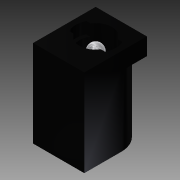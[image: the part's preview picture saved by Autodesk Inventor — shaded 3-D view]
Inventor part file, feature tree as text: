
AUTODESK INVENTOR PART (.ipt)
format: ipt  version: 2014 SP1 (Build 180222100, 222)  size: 133,632 bytes
history: native  units: mm
features: extrude x5, sketch x5, fillet x1
ambient origin geometry x8: Origin, YZ Plane, XZ Plane, XY Plane, X Axis, Y Axis, Z Axis, Center Point
bodies: Solid1 (feature_tree)
feature tree (11):
  extrude  "Extrusion1"  TaperAngle=0.0deg  [1 undecoded]
  extrude  "Extrusion2"  Depth=4.5mm
  extrude  "Extrusion4"  Depth=15.3mm
  extrude  "Extrusion3"  Depth=10.0mm TaperAngle=0.0deg
  fillet  "Fillet1"  Radius=2.5mm
  extrude  "Extrusion5"  Depth=1.25mm
  sketch  "Sketch1"  dims[d0=9.0mm d1=0.0mm]
  sketch  "Sketch2"  dims[d2=11.0mm d3=4.5mm]
  sketch  "Sketch3"  dims[d4=15.3mm d5=0.0mm d6=5.7mm]
  sketch  "Sketch4"  dims[d7=6.5mm d8=10.0mm d9=0.0mm d10=2.5mm]
  sketch  "Sketch5"  dims[d11=9.0mm d12=0.0mm d13=1.25mm d14=7.0mm d15=1.5mm d16=1.5mm d17=3.5mm d18=3.0mm d19=1.5mm d20=2.0mm d21=0.0mm d22=0.0mm d23=9.0mm d24=12.3mm d25=0.0mm]
note: 1 required parameter value undecoded (feature->parameter linkage not recoverable at this tier; creation-order binding heuristic only, values carry confidence <= 0.55)
